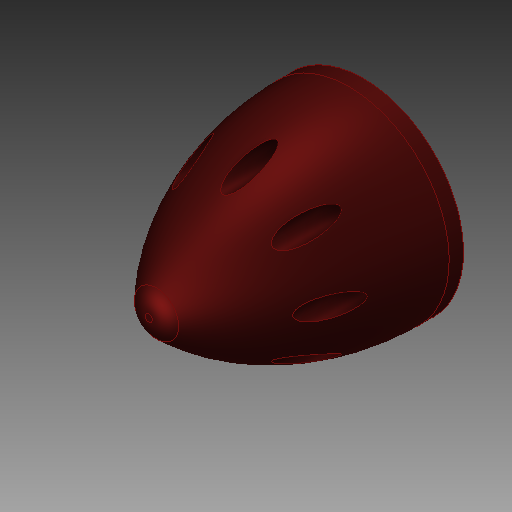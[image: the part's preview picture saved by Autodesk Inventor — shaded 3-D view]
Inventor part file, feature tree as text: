
AUTODESK INVENTOR PART (.ipt)
format: ipt  version: 2019 (Build 230136000, 136)  size: 325,120 bytes
history: native  units: mm
features: sketch x5, extrude x2, revolve x1, fillet x1, hole x1, plane x1, pattern_circular x1
ambient origin geometry x8: Origin, YZ Plane, XZ Plane, XY Plane, X Axis, Y Axis, Z Axis, Center Point
bodies: Solid1 (feature_tree)
feature tree (12):
  revolve  "Revolution1"  [1 undecoded]
  fillet  "Fillet1"  Radius=5.0mm
  hole  "Hole1"  [1 undecoded]
  extrude  "Extrusion1"  TaperAngle=90.0deg  [1 undecoded]
  plane  "Work Plane1"
  sketch  "Sketch4"  dims[d7=9.0mm d8=28.0mm]
  extrude  "Extrusion2"  Depth=28.0mm
  pattern_circular  "Circular Pattern1"  [2 undecoded]
  sketch  "Sketch1"  dims[d0=75.0mm d1=70.0mm d2=5.0mm]
  sketch  "Sketch2"  dims[d3=5.0mm d4=15.0mm]
  sketch  "Sketch3"  dims[d5=2.0mm d6=90.0deg]
  sketch  "Sketch5"  dims[d9=4.0mm d10=6.0mm d11=4.0mm d12=2.0mm d13=90.0deg d14=8.0mm d15=20.594885mm d16=10.0mm d17=10.0mm d18=0.0mm d19=80.0mm d20=360.0deg d22=9.0mm d23=-5.0mm d24=7.25mm d25=10.0mm d26=0.0mm]
note: 5 required parameter values undecoded (feature->parameter linkage not recoverable at this tier; creation-order binding heuristic only, values carry confidence <= 0.55)